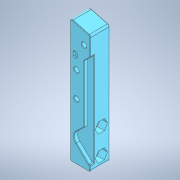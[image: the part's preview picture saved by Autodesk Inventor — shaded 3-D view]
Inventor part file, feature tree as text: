
AUTODESK INVENTOR PART (.ipt)
format: ipt  version: 2021.2 (Build 252289000, 289)  size: 388,608 bytes
history: native  units: mm
features: other x4, chamfer x4, fillet x3
ambient origin geometry x8: Origin, YZ Plane, XZ Plane, XY Plane, X Axis, Y Axis, Z Axis, Center Point
bodies: Body1 (feature_tree)
feature tree (11):
  other  "Твёрдое тело.ipt"
  fillet  "Сопряжение1"  Radius=10.0mm
  chamfer  "Фаска1"  Distance=2.0mm
  chamfer  "Фаска2"  Distance=0.5mm Angle=45.0deg
  chamfer  "Фаска3"  Distance=0.5mm Angle=45.0deg
  fillet  "Сопряжение3"  Radius=0.5mm
  fillet  "Сопряжение2"  Radius=0.5mm
  chamfer  "Фаска4"  Distance=1.0mm Angle=45.0deg
  other  "Ножка левая низ::Твёрдое тело.ipt"
  other  "Элемент создания тегов1"
  other  "Твердое тело1"
